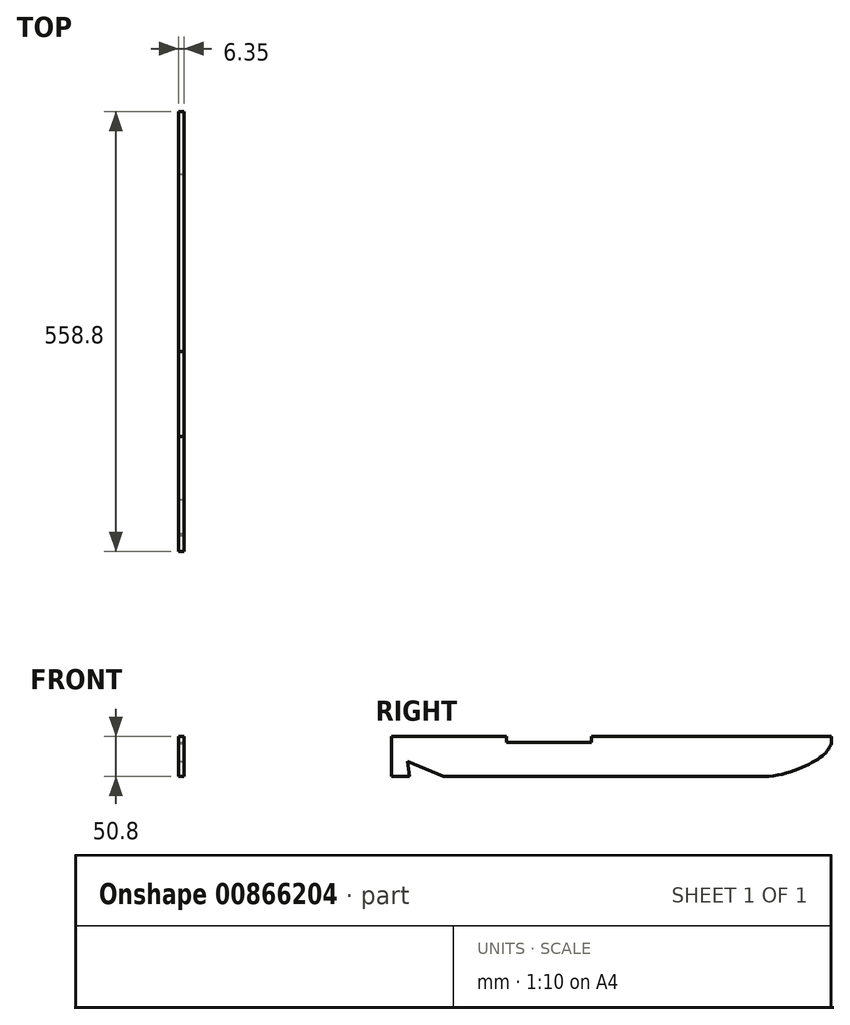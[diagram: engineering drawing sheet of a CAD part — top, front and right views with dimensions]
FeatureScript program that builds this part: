
annotation { "Feature Type Name" : "Feature", "Feature Type Description" : "" }
export const myFeature = defineFeature(function(context is Context, id is Id, definition is map)
    precondition{}
    {
        {
            var Q0;
            Q0=qCreatedBy(makeId("Front.planeOp"),FACE);
            var sketch = newSketch(context, id + "F0", { "sketchPlane" : qUnion([Q0])});
            skLineSegment(sketch, "E0.bottom", {"start": v(0, 0) * mm, "end": v(-6.35, 0) * mm});
            skLineSegment(sketch, "E0.top", {"start": v(0, -50.8) * mm, "end": v(-6.35, -50.8) * mm});
            skLineSegment(sketch, "E0.left", {"start": v(0, 0) * mm, "end": v(0, -50.8) * mm});
            skLineSegment(sketch, "E0.right", {"start": v(-6.35, 0) * mm, "end": v(-6.35, -50.8) * mm});
            skSolve(sketch);
        }
        {
            var Q0;
            Q0=makeQuery(id+"F0.imprint","IMPRINT",FACE,{"disambiguationData":[TD([[makeQuery(id+"F0.imprint","IMPRINT",EDGE,{"derivedFrom":sQuery(id+"F0.wireOp",EDGE,"E0.bottom")}),1.0]])]});
            extrude(context, id + "F1", {"entities" : qUnion([Q0]), "depth" : 558.8 * mm, "offsetDistance" : 25.4 * mm});
        }
        {
            var Q0;
            Q0=makeQuery(id+"F1.opExtrude","SWEPT_FACE",FACE,{"disambiguationData":[OSD([sQuery(id+"F0.wireOp",EDGE,"E0.left")])]});
            var sketch = newSketch(context, id + "F2", { "sketchPlane" : qUnion([Q0])});
            skLineSegment(sketch, "E1", {"start": v(-536.18, -50.8) * mm, "end": v(-538.38, -31.91) * mm});
            skLineSegment(sketch, "E2", {"start": v(-538.38, -31.91) * mm, "end": v(-492.82, -50.8) * mm});
            skSolve(sketch);
        }
        {
            var Q0;
            {var subQ0=sQuery(id+"F2.wireOp",EDGE,"E1");Q0=makeQuery(id+"F2.imprint","IMPRINT",FACE,{"disambiguationData":[TD([[makeQuery(id+"F2.imprint","IMPRINT",EDGE,{"derivedFrom":subQ0}),-1.0]])]});}
            extrude(context, id + "F3", {"entities" : qUnion([Q0]), "operationType" : NewBodyOperationType.REMOVE, "oppositeDirection" : true, "depth" : 304.8 * mm, "offsetDistance" : 25.4 * mm});
        }
        {
            var Q0;
            Q0=makeQuery(id+"F1.opExtrude","SWEPT_FACE",FACE,{"disambiguationData":[OSD([sQuery(id+"F0.wireOp",EDGE,"E0.left")])]});
            var sketch = newSketch(context, id + "F4", { "sketchPlane" : qUnion([Q0])});
            skLineSegment(sketch, "E3", {"start": v(-412.75, 0) * mm, "end": v(-412.75, -7.62) * mm});
            skLineSegment(sketch, "E4", {"start": v(-412.75, -7.62) * mm, "end": v(-304.8, -7.62) * mm});
            skLineSegment(sketch, "E5", {"start": v(-304.8, -7.62) * mm, "end": v(-304.8, 0) * mm});
            skLineSegment(sketch, "E6", {"start": v(-412.75, -7.62) * mm, "end": v(-558.8, -7.62) * mm});
            skSolve(sketch);
        }
        {
            var Q0;
            {var subQ0=sQuery(id+"F4.wireOp",EDGE,"E3");Q0=makeQuery(id+"F4.imprint","IMPRINT",FACE,{"disambiguationData":[TD([[makeQuery(id+"F4.imprint","IMPRINT",EDGE,{"derivedFrom":subQ0}),1.0]])]});}
            extrude(context, id + "F5", {"entities" : qUnion([Q0]), "operationType" : NewBodyOperationType.REMOVE, "oppositeDirection" : true, "depth" : 304.8 * mm, "offsetDistance" : 25.4 * mm});
        }
        {
            var Q0;
            Q0=makeQuery(id+"F1.opExtrude","SWEPT_FACE",FACE,{"disambiguationData":[OSD([sQuery(id+"F0.wireOp",EDGE,"E0.left")])]});
            var sketch = newSketch(context, id + "F6", { "sketchPlane" : qUnion([Q0])});
            skFitSpline(sketch, "E7", {"points": [v(0, -8.7) * mm, v(-10.95, -24.2) * mm, v(-79.24, -50.8) * mm], "startDerivative": vector(-19.59, -49.34) * mm, "endDerivative": vector(-127.59, -13.23) * mm});
            skSolve(sketch);
        }
        {
            var Q0;
            {var subQ0=sQuery(id+"F6.wireOp",EDGE,"E7");Q0=makeQuery(id+"F6.imprint","IMPRINT",FACE,{"disambiguationData":[TD([[makeQuery(id+"F6.imprint","IMPRINT",EDGE,{"derivedFrom":subQ0}),1.0]])]});}
            extrude(context, id + "F7", {"entities" : qUnion([Q0]), "operationType" : NewBodyOperationType.REMOVE, "oppositeDirection" : true, "depth" : 25.4 * mm, "offsetDistance" : 25.4 * mm});
        }
    });
